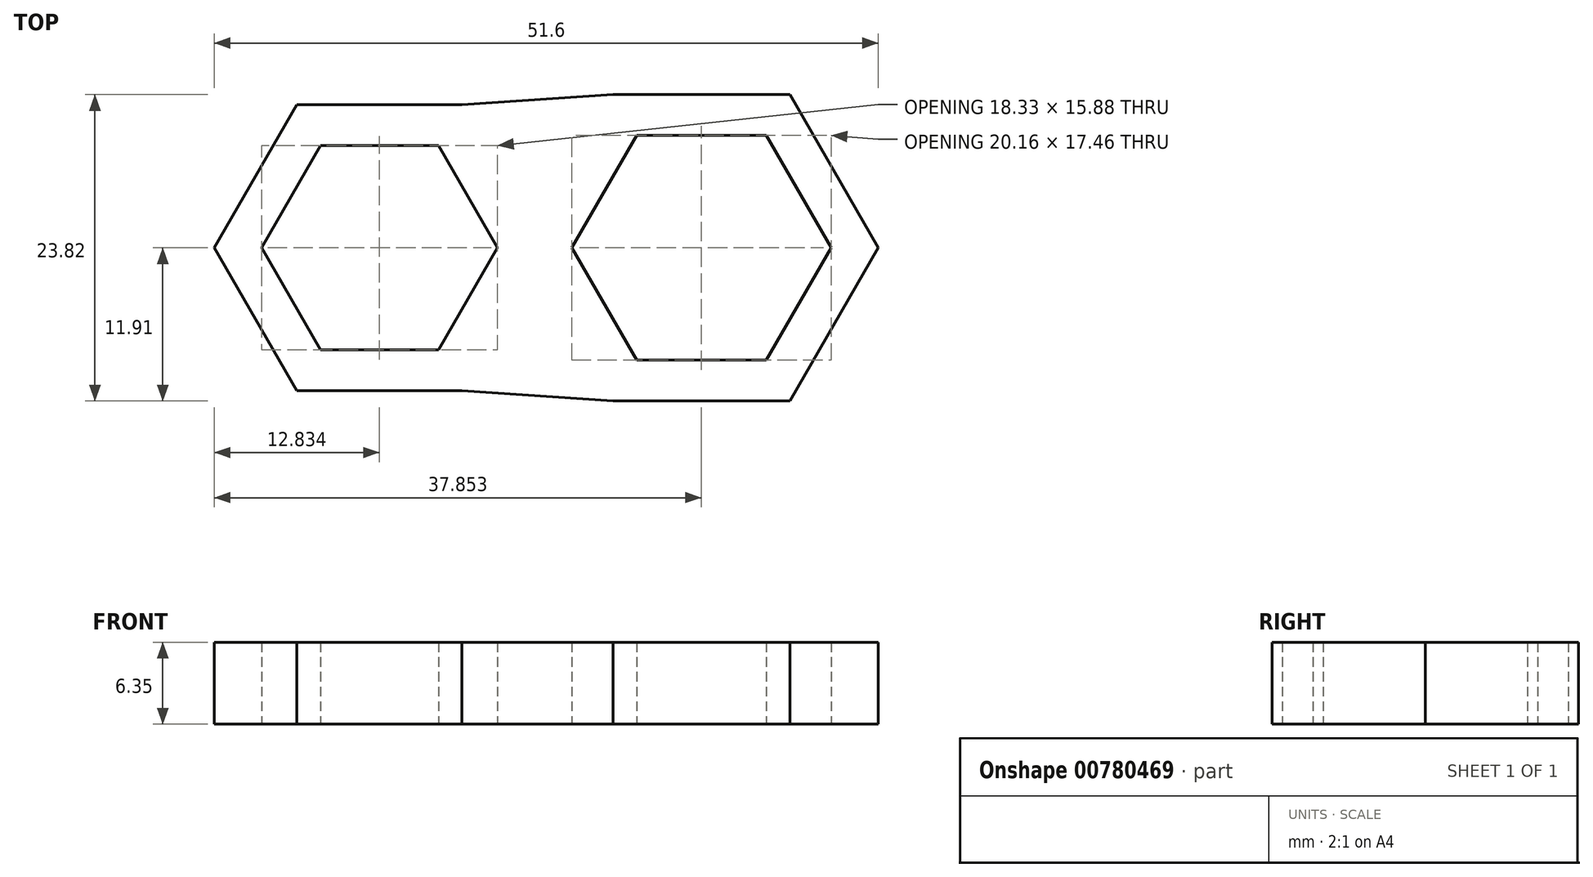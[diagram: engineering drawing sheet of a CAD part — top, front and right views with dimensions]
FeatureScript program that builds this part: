
annotation { "Feature Type Name" : "Feature", "Feature Type Description" : "" }
export const myFeature = defineFeature(function(context is Context, id is Id, definition is map)
    precondition{}
    {
        {
            var Q0;
            Q0=qCreatedBy(makeId("Top.planeOp"),FACE);
            var sketch = newSketch(context, id + "F0", { "sketchPlane" : qUnion([Q0])});
            skCircle(sketch, "E0.cCircle", {"center": v(-16.07, 0) * mm, "radius": 7.94 * mm, "construction": true});
            skLineSegment(sketch, "E0.0", {"start": v(-11.48, -7.94) * mm, "end": v(-20.65, -7.94) * mm});
            skLineSegment(sketch, "E0.1", {"start": v(-20.65, -7.94) * mm, "end": v(-25.23, 0) * mm});
            skLineSegment(sketch, "E0.2", {"start": v(-25.23, 0) * mm, "end": v(-20.65, 7.94) * mm});
            skLineSegment(sketch, "E0.3", {"start": v(-20.65, 7.94) * mm, "end": v(-11.48, 7.94) * mm});
            skLineSegment(sketch, "E0.4", {"start": v(-11.48, 7.94) * mm, "end": v(-6.9, 0) * mm});
            skLineSegment(sketch, "E0.5", {"start": v(-6.9, 0) * mm, "end": v(-11.48, -7.94) * mm});
            skPoint(sketch, "E0.0.midPoint", {"position": v(-16.07, -7.94) * mm});
            skCircle(sketch, "E1.cCircle", {"center": v(8.95, 0) * mm, "radius": 8.73 * mm, "construction": true});
            skLineSegment(sketch, "E1.0", {"start": v(14, -8.73) * mm, "end": v(3.91, -8.73) * mm});
            skLineSegment(sketch, "E1.1", {"start": v(3.91, -8.73) * mm, "end": v(-1.13, 0) * mm});
            skLineSegment(sketch, "E1.2", {"start": v(-1.13, 0) * mm, "end": v(3.91, 8.73) * mm});
            skLineSegment(sketch, "E1.3", {"start": v(3.91, 8.73) * mm, "end": v(14, 8.73) * mm});
            skLineSegment(sketch, "E1.4", {"start": v(14, 8.73) * mm, "end": v(19.04, 0) * mm});
            skLineSegment(sketch, "E1.5", {"start": v(19.04, 0) * mm, "end": v(14, -8.73) * mm});
            skPoint(sketch, "E1.0.midPoint", {"position": v(8.95, -8.73) * mm});
            skCircle(sketch, "E2.cCircle", {"center": v(-16.07, 0) * mm, "radius": 11.11 * mm, "construction": true});
            skLineSegment(sketch, "E2.0", {"start": v(-9.65, -11.11) * mm, "end": v(-22.48, -11.11) * mm});
            skLineSegment(sketch, "E2.1", {"start": v(-22.48, -11.11) * mm, "end": v(-28.9, 0) * mm});
            skLineSegment(sketch, "E2.2", {"start": v(-28.9, 0) * mm, "end": v(-22.48, 11.11) * mm});
            skLineSegment(sketch, "E2.3", {"start": v(-22.48, 11.11) * mm, "end": v(-9.65, 11.11) * mm});
            skLineSegment(sketch, "E2.4", {"start": v(-9.65, 11.11) * mm, "end": v(-3.23, 0) * mm});
            skLineSegment(sketch, "E2.5", {"start": v(-3.23, 0) * mm, "end": v(-9.65, -11.11) * mm});
            skPoint(sketch, "E2.0.midPoint", {"position": v(-16.07, -11.11) * mm});
            skCircle(sketch, "E3.cCircle", {"center": v(8.95, 0) * mm, "radius": 11.9 * mm, "construction": true});
            skLineSegment(sketch, "E3.0", {"start": v(15.83, -11.9) * mm, "end": v(2.08, -11.9) * mm});
            skLineSegment(sketch, "E3.1", {"start": v(2.08, -11.9) * mm, "end": v(-4.8, 0) * mm});
            skLineSegment(sketch, "E3.2", {"start": v(-4.8, 0) * mm, "end": v(2.08, 11.9) * mm});
            skLineSegment(sketch, "E3.3", {"start": v(2.08, 11.9) * mm, "end": v(15.83, 11.9) * mm});
            skLineSegment(sketch, "E3.4", {"start": v(15.83, 11.9) * mm, "end": v(22.7, 0) * mm});
            skLineSegment(sketch, "E3.5", {"start": v(22.7, 0) * mm, "end": v(15.83, -11.9) * mm});
            skPoint(sketch, "E3.0.midPoint", {"position": v(8.95, -11.9) * mm});
            skLineSegment(sketch, "E4", {"start": v(-9.65, 11.11) * mm, "end": v(2.08, 11.9) * mm});
            skLineSegment(sketch, "E5", {"start": v(-9.65, -11.11) * mm, "end": v(2.08, -11.9) * mm});
            skSolve(sketch);
        }
        {
            var Q0;
            Q0=makeQuery(id+"F0.imprint","IMPRINT",FACE,{"disambiguationData":[TD([[makeQuery(id+"F0.imprint","IMPRINT",EDGE,{"derivedFrom":sQuery(id+"F0.wireOp",EDGE,"E0.0")}),1.0]])]});
            var Q1;
            {var subQ0=sQuery(id+"F0.wireOp",EDGE,"E4");Q1=makeQuery(id+"F0.imprint","IMPRINT",FACE,{"disambiguationData":[TD([[makeQuery(id+"F0.imprint","IMPRINT",EDGE,{"derivedFrom":subQ0}),-1.0]])]});}
            var Q2;
            {var subQ0=sQuery(id+"F0.wireOp",EDGE,"E5");Q2=makeQuery(id+"F0.imprint","IMPRINT",FACE,{"disambiguationData":[TD([[makeQuery(id+"F0.imprint","IMPRINT",EDGE,{"derivedFrom":subQ0}),1.0]])]});}
            var Q3;
            Q3=makeQuery(id+"F0.imprint","IMPRINT",FACE,{"disambiguationData":[TD([[makeQuery(id+"F0.imprint","IMPRINT",EDGE,{"derivedFrom":sQuery(id+"F0.wireOp",EDGE,"E1.0")}),1.0]])]});
            var Q4;
            {var subQ0=sQuery(id+"F0.wireOp",EDGE,"E2.5");var subQ1=sQuery(id+"F0.wireOp",EDGE,"E2.4");var subQ2=makeQuery(id+"F0.imprint","INTERSECT",VERTEX,{"derivedFrom":[subQ1,subQ0]});Q4=makeQuery(id+"F0.imprint","IMPRINT",FACE,{"disambiguationData":[TD([[makeQuery(id+"F0.imprint","IMPRINT",EDGE,{"disambiguationData":[TD([[subQ2,1.0]])],"derivedFrom":subQ1}),-1.0]])]});}
            extrude(context, id + "F1", {"entities" : qUnion([Q0, Q1, Q2, Q3, Q4]), "depth" : 6.35 * mm, "offsetDistance" : 25.4 * mm});
        }
    });
